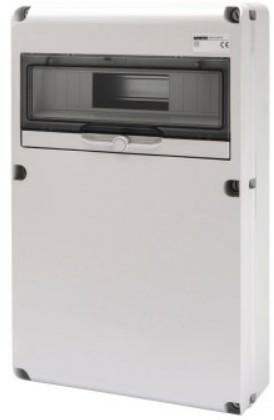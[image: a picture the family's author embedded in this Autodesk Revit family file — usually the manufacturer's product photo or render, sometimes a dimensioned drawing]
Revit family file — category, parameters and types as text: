
# Revit family: Building-IEC309Boards-GEWISS-68QDIN-DISTRIBUTION-BOARD-14MOD_BLANK_DOUBLE
name_source: partatom
category: Apparecchi elettrici
units: mm (PartAtom-declared; Revit-internal decimal feet)

## family parameters
Condiviso = No
Host = Superficie
Mantenere orientamento annotazione = Sì
Punto di calcolo locali = Sì
Quota connettore circolare = Usa diametro
Taglio con vuoti quando caricato = No
Tipo di parte = Normale

## types (1)
- GW68007N - Q-DIN 14M.BLIND COV. 510X320X135 IP65
    Accordance with Standards = EN 60208 - EN 60670-1 - IEC 60670-24
    Catalogue = BUILDING
    Catalogue Range = 68 QDIN
    Colour = Grey RAL 7035
    Descrizione = Q-DIN 14M.BLIND COV. 510X320X135 IP65
    Dispersible power A (W) = 24
    Dispersible power B (W) = 64
    EAN code = 8011564744783
    Electrocod = 2242
    Glow Wire Test = 650°C
    Houseable socket = Blank lid
    IDF = dbb83824-73e0-496e-9ba5-1c5fa3188cb8
    IDT = 5858c0d8-961a-4254-a97b-2dfffa1f665c
    IP degree = IP65
    Immagine tipo = GW68007N.jpg
    Installation type = Surface-mounting
    Insulation class = II
    L_Moduli = 266 mm  [stored 0.872703 ft]
    Modello = GW68007N
    N_Moduli = 14 mm  [stored 0.0459318 ft]
    No. of modules EN 50022 = 14
    No. of provided blank lids = -
    Operating temperature: = -25 +40 °C
    POMELLO = bianco
    PRESA = rosso
    Produttore = GEWISS S.p.A.
    Prospetto di default = 1219 mm
    SEO = Board
    STRUTTURA = RAL - 7035
    STRUTTURA ALTA = Poche
    Shock resistance = IK09
    Spostamento_S = 1000 mm  [stored 3.28084 ft]
    Technical sheet = https://www.gewiss.com
    Thermo-pressure with ball = 70
    URL = https://www.gewiss.com
    VETRO = Vetro
    Version file RFA = 21.5
    Version type = Empty

note: source unit labels omitted for Thermo-pressure with ball — the stored unit's dimension contradicts the parameter name (converter mislabeling)

note: [stored X ft] marks values corroborated as IEEE doubles in the binary element streams (Revit-internal decimal feet)

## geometry (parser evidence)
native form markers: Sweep x3
no freeform markers — native parametric forms only
